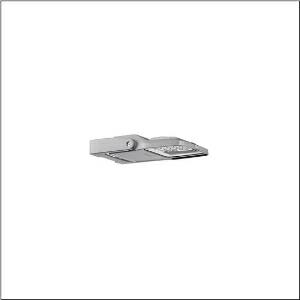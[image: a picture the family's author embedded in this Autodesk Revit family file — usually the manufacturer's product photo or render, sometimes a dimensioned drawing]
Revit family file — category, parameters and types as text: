
# Revit family: floodlight_fl_21_micro___pl33t_5xa7762a2f2a_86f6
name_source: partatom
category: Lighting Fixtures
units: mm (PartAtom-declared; Revit-internal decimal feet)

## family parameters
Cut with Voids When Loaded = No
Host = Face
Light Source = No
Part Type = Normal
Room Calculation Point = No
Round Connector Dimension = Use Diameter
Shared = No

## types (1)
- --- (1 x LED, 2930 lm, 23.1 W, 3000K)
    Apparent Load = 23 VA
    CIE Flux Codes = 26 75 99 100 100
    Color Rendering = 70
    Color Temperature = 3000K
    Default Elevation = 1800 mm
    Description = Floodlight FL 21 micro, floodlight, primary light control with lens, of PMMA, primary optical cover: protective disc, of toughened safety glass, transparent, light distribution: PL33T, light emission: direct distribution, installation type: surface-mounted, LED, High Power LED, rated luminous flux: 2.930lm, luminous efficacy: 127lm/W, light colour: 730, colour temperature: 3000K, control gear: ECG iQ, control: Auto-Match, Temp-Guard, Night-Set, Smart-Wire, Desk-Remote (wireless, voltage-free reading and setting of iQ features in the workshop via application-optimized NFC function/RFID function), optimised constant luminous flux control (CLO 2.0), Street-Remote, with terminal, 6-pole, mains connection: 220..240V, AC, 50/60Hz, start of lifetime: 23W, end of lifetime: 24W, reduction: 11W, luminaire housing, of diecast aluminium, powder-coated, Siteco® metallic grey (DB 702S), corrosivity category C5 according to DIN EN ISO 12944, design bracket, of diecast aluminium, powder-coated, Siteco® metallic grey (DB 702S), protection rating (complete): IP66, insulation class (complete): insulation class II (safety insulation), certification: CE, protection symbol: D, impact resistance: IK07, permissible operating ambient temperature: -40..+40°C, permissible operating ambient temperature for outdoor applications: -40..+50°C, standard: DIN EN 12944, packaging unit: 1 piece

Light Distribution: PL33T
    Height = 65 mm
    Lamp = 1 x LED
    Lamp Light Flux = 2930 lm
    Lamp Power = 23.1 W
    Lamp count = 1
    Length = 312 mm
    Luminous efficacy = 127 lm/W
    Manufacturer = Siteco
    ModVariant = No
    Model = 5XA7762A2F2A
    Number of Poles = 1
    OnlyDefault = Yes
    Power Factor = 1
    Product Name = Floodlight FL 21 micro | PL33T
    Product group = floodlight | pylon top
    ProductGroupID = 6101
    Protection Class = Protection class II
    Protection Degree = IP 66
    RLX_Detail_Level = 1
    RlxData = <blob elided: 97373 chars, md5=28e54a88>
    Socket = socket
    Standby Power = 0 W
    System Light Flux = 2930 lm
    System Power = 23 W
    Type Comments = factory setting: luminous flux: 100 % | dim-lin: 254 | 455 mA
    Type Image = l_1006878.jpg
    URL = http://relux.com
    VarID = @adj_058099
    Voltage = 0 V
    Weight = 0.00 kg
    Width = 230 mm

## geometry (parser evidence)
native form markers: Blend x4, Sweep x13
no freeform markers — native parametric forms only
